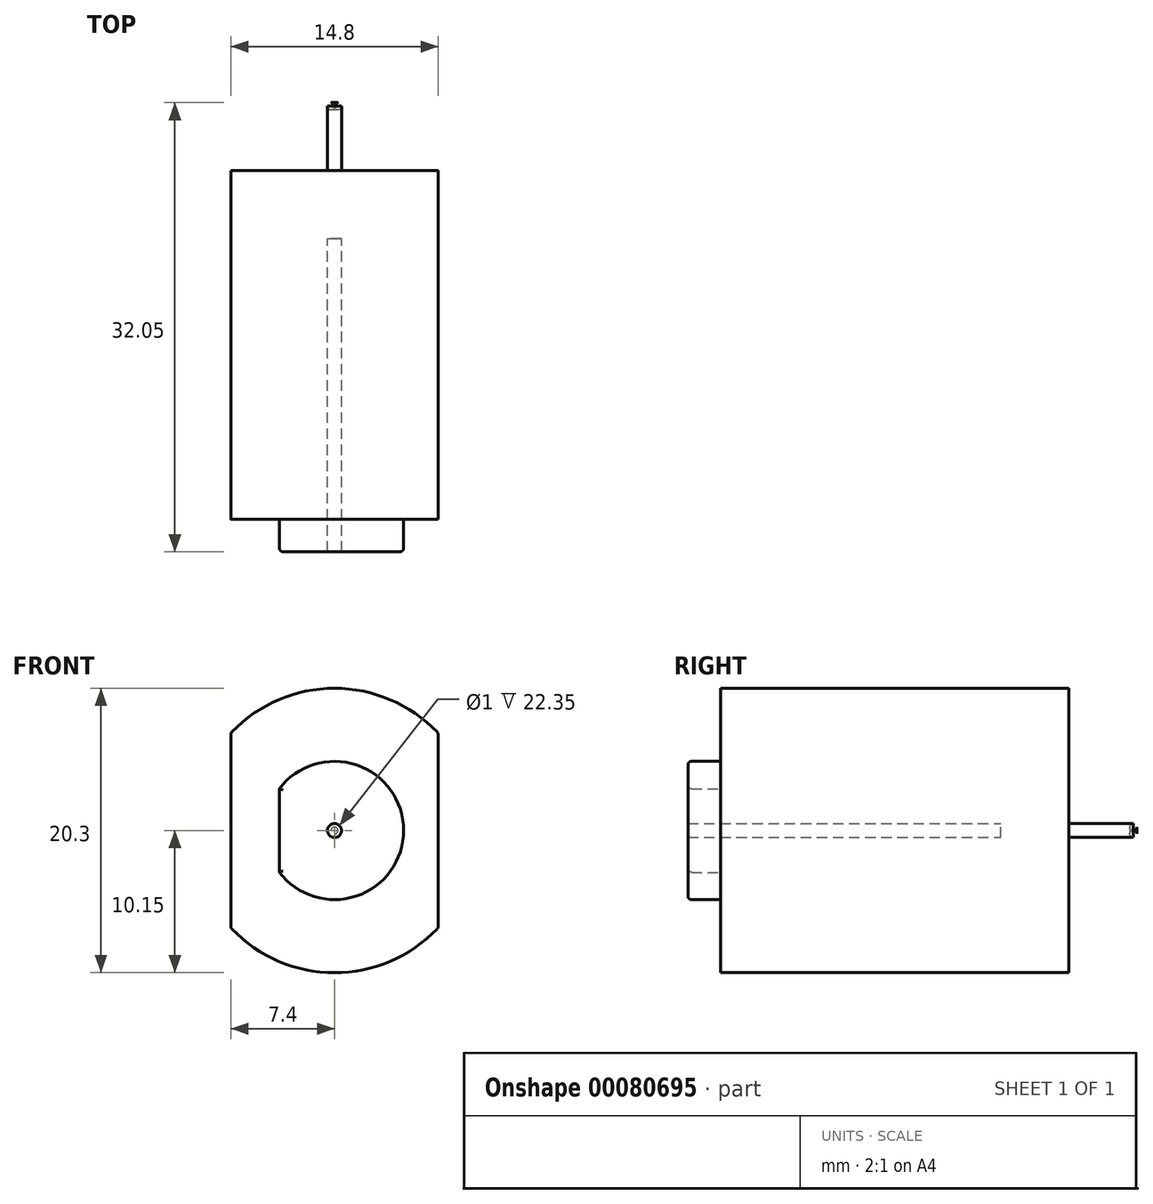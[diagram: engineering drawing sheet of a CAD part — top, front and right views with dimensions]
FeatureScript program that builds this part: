
annotation { "Feature Type Name" : "Feature", "Feature Type Description" : "" }
export const myFeature = defineFeature(function(context is Context, id is Id, definition is map)
    precondition{}
    {
        {
            var Q0;
            Q0=qCreatedBy(makeId("Front.planeOp"),FACE);
            var sketch = newSketch(context, id + "F0", { "sketchPlane" : qUnion([Q0])});
            skArc(sketch, "E0", {"start": v(-7.4, -6.95) * mm, "mid": v(0, -10.15) * mm, "end": v(7.4, -6.95) * mm});
            skLineSegment(sketch, "E1", {"start": v(-7.4, 6.95) * mm, "end": v(-7.4, -6.95) * mm});
            skLineSegment(sketch, "E2.MirrorCS", {"start": v(7.4, 6.95) * mm, "end": v(7.4, -6.95) * mm});
            skArc(sketch, "E3.trimOffspring", {"start": v(7.4, 6.95) * mm, "mid": v(0, 10.15) * mm, "end": v(-7.4, 6.95) * mm});
            skArc(sketch, "E4", {"start": v(-3.94, -2.98) * mm, "mid": v(4.93, 0) * mm, "end": v(-3.94, 2.98) * mm});
            skLineSegment(sketch, "E5", {"start": v(-3.94, -2.98) * mm, "end": v(-3.94, 2.98) * mm});
            skCircle(sketch, "E6", {"center": v(0, 0) * mm, "radius": 0.5 * mm});
            skSolve(sketch);
        }
        {
            var Q0;
            Q0=makeQuery(id+"F0.imprint","IMPRINT",FACE,{"disambiguationData":[TD([[makeQuery(id+"F0.imprint","IMPRINT",EDGE,{"derivedFrom":sQuery(id+"F0.wireOp",EDGE,"E0")}),1.0]])]});
            extrude(context, id + "F1", {"entities" : qUnion([Q0]), "depth" : 24.87 * mm});
        }
        {
            var Q0;
            Q0=makeQuery(id+"F0.imprint","IMPRINT",FACE,{"disambiguationData":[TD([[makeQuery(id+"F0.imprint","IMPRINT",EDGE,{"derivedFrom":sQuery(id+"F0.wireOp",EDGE,"E4")}),1.0]])]});
            extrude(context, id + "F2", {"entities" : qUnion([Q0]), "operationType" : NewBodyOperationType.ADD, "depth" : 27.2 * mm});
        }
        {
            var Q0;
            Q0=makeQuery(id+"F0.imprint","IMPRINT",FACE,{"disambiguationData":[TD([[makeQuery(id+"F0.imprint","IMPRINT",EDGE,{"derivedFrom":sQuery(id+"F0.wireOp",EDGE,"E6")}),1.0]])]});
            extrude(context, id + "F3", {"entities" : qUnion([Q0]), "operationType" : NewBodyOperationType.ADD, "depth" : 9.7 * mm, "symmetric" : true});
        }
        {
            var Q0;
            Q0=makeQuery(id+"F2.opExtrude","CAP_EDGE",EDGE,{"disambiguationData":[OSD([sQuery(id+"F0.wireOp",EDGE,"E5")])],"isStart":false});
            var Q1;
            Q1=makeQuery(id+"F2.opExtrude","CAP_EDGE",EDGE,{"disambiguationData":[OSD([sQuery(id+"F0.wireOp",EDGE,"E4")])],"isStart":false});
            var Q2;
            Q2=makeQuery(id+"F1.opExtrude","SWEPT_EDGE",EDGE,{"disambiguationData":[OSD([sQuery(id+"F0.wireOp",EDGE,"E0"),sQuery(id+"F0.wireOp",EDGE,"E2.MirrorCS")])]});
            var Q3;
            Q3=makeQuery(id+"F1.opExtrude","SWEPT_EDGE",EDGE,{"disambiguationData":[OSD([sQuery(id+"F0.wireOp",EDGE,"E2.MirrorCS"),sQuery(id+"F0.wireOp",EDGE,"E3.trimOffspring")])]});
            var Q4;
            Q4=makeQuery(id+"F1.opExtrude","SWEPT_EDGE",EDGE,{"disambiguationData":[OSD([sQuery(id+"F0.wireOp",EDGE,"E1"),sQuery(id+"F0.wireOp",EDGE,"E3.trimOffspring")])]});
            var Q5;
            Q5=makeQuery(id+"F1.opExtrude","SWEPT_EDGE",EDGE,{"disambiguationData":[OSD([sQuery(id+"F0.wireOp",EDGE,"E0"),sQuery(id+"F0.wireOp",EDGE,"E1")])]});
            var Q6;
            Q6=makeQuery(id+"F3.opExtrude","CAP_FACE",FACE,{"disambiguationData":[OSD([sQuery(id+"F0.wireOp",EDGE,"E6")])],"isStart":true});
            fillet(context, id + "F4", {"entities" : qUnion([Q0, Q1, Q2, Q3, Q4, Q5, Q6]), "radius" : 0.25 * mm, "tangentPropagation" : true, "allowEdgeOverflow" : false});
        }
    });
